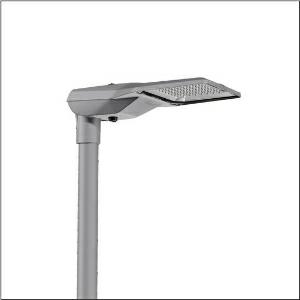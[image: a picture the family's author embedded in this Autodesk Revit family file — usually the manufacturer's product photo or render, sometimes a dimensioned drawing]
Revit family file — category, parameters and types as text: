
# Revit family: streetlight_sl_21_midi___st1_0a_5xe3d43t08lb_efa2
name_source: partatom
category: Lighting Fixtures
units: mm (PartAtom-declared; Revit-internal decimal feet)

## family parameters
Cut with Voids When Loaded = No
Host = Face
Light Source = No
Part Type = Normal
Room Calculation Point = No
Round Connector Dimension = Use Diameter
Shared = No

## types (1)
- --- (1 x LED, 14950 lm, 99.6 W, 4000K)
    Apparent Load = 100 VA
    CIE Flux Codes = 37 72 97 100 100
    Color Rendering = 70
    Color Temperature = 4000K
    Default Elevation = 1800 mm
    Description = Streetlight SL 21 midi, mast luminaire, primary light control with lens, of PMMA, primary optical cover: cover, of toughened safety glass, transparent, light distribution: ST1.0a, light emission: direct distribution, primary light characteristic: asymmetric, installation type: side-entry, post-top, LED, High Power LED, rated luminous flux: 14.950lm, luminous efficacy: 150lm/W, light colour: 740, colour temperature: 4000K, control gear: D4i, control: overheat protection, constant luminous flux control, time-dependent luminous flux control, flexible luminous flux parameterisation, pre-setting: logarithmic dimming characteristic, mains connection: 230..240V, AC, 50/60Hz, start of lifetime: 100W, end of service life: 102W, reduction: 46W, luminaire housing, of diecast aluminium, powder-coated, SITECO metallic grey (DB 702S), corrosivity category C5 high according to DIN EN ISO 12944, please order mast flange separately, inclination adjustable: 0°, 5°, 10°, 15°, sealing non-destructively replaceable, multi-level sealing system, length: 644mm, width: 335mm, height: 110mm, mast flange for spigot size: 42mm (side-entry): 5XC10008XM4, 60/48mm (side-entry/post-top): 5XC10108XM2, 76/60mm (side-entry/post-top): 5XC10108XM1, mounting height: 4..8m, Smart Interface below and above, protection rating (complete): IP66, insulation class (complete): insulation class II (safety insulation), certification: CE, ENEC, ENEC+, VDE, impact resistance: IK10, permissible operating ambient temperature for outdoor applications: -40..+50°C, standard-compliant lighting for roads and squares, packaging unit: 1 piece

Light Distribution: ST1.0a
    Height = 111 mm
    Lamp = 1 x LED
    Lamp Light Flux = 14950 lm
    Lamp Power = 99.6 W
    Lamp count = 1
    Length = 644 mm
    Luminous efficacy = 150 lm/W
    Manufacturer = Siteco
    ModVariant = No
    Model = 5XE3D43T08LB
    Number of Poles = 1
    OnlyDefault = Yes
    Power Factor = 1
    Product Name = Streetlight SL 21 midi | ST1.0a
    Product group = mast luminaire | pylon top
    ProductGroupID = 6100
    Protection Class = Protection class II
    Protection Degree = IP 66
    RLX_Detail_Level = 1
    RLX_Emergency_Light_Flux = 0 lm
    RLX_Emergency_Type = 0
    RLX_Emergency_Type_DB = No
    RlxData = <blob elided: 26881 chars, md5=9e1ff8fa>
    Socket = socket
    Standby Power = 0 W
    System Light Flux = 14950 lm
    System Power = 100 W
    Type Comments = factory setting: luminous flux: 100 % | dim-lin: 254 | 1020 mA
    Type Image = l_1004304.jpg
    URL = http://relux.com
    VarID = @adj_031767
    Voltage = 0 V
    Weight = 0.00 kg
    Width = 336 mm

## geometry (parser evidence)
native form markers: Blend x4, Sweep x12
no freeform markers — native parametric forms only
